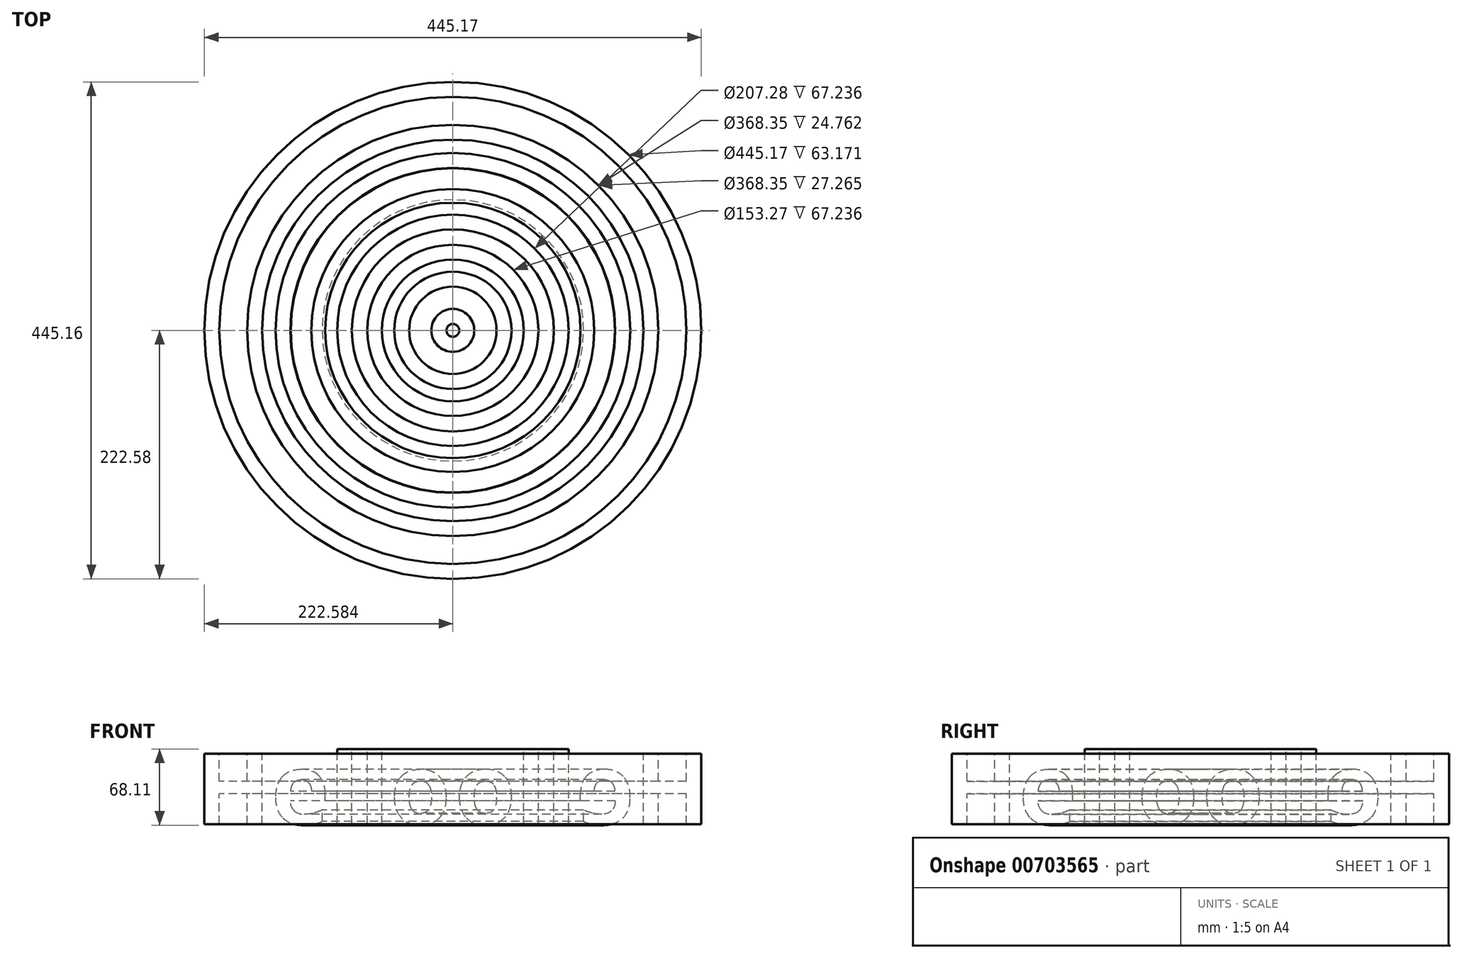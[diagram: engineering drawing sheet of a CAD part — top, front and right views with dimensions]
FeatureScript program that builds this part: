
annotation { "Feature Type Name" : "Feature", "Feature Type Description" : "" }
export const myFeature = defineFeature(function(context is Context, id is Id, definition is map)
    precondition{}
    {
        {
            var Q0;
            Q0=qCreatedBy(makeId("Front.planeOp"),FACE);
            var sketch = newSketch(context, id + "F0", { "sketchPlane" : qUnion([Q0])});
            skText(sketch, "E0", { "text": "Hello", "fontName": "OpenSans-Bold.ttf"});
            const initialGuessF0  = {"E0": [-0.11498, -0.02415, 1, 0, 0.06371]};
            skSetInitialGuess(sketch, initialGuessF0);
            skSolve(sketch);
        }
        {
            var Q0;
            Q0 = qConstructionFilter(qBodyType(qCreatedBy(id + "F0" ,EDGE), BodyType.WIRE), ConstructionObject.NO);
            var Q1;
            Q1=sQuery(id+"F0.wireOp",EDGE,"E0.sketch_text.right");
            revolve(context, id + "F1", {"bodyType" : ToolBodyType.SURFACE, "surfaceOperationType" : NewSurfaceOperationType.NEW, "surfaceEntities" : qUnion([Q0]), "axis" : qUnion([Q1]), "revolveType" : RevolveType.FULL});
        }
    });
